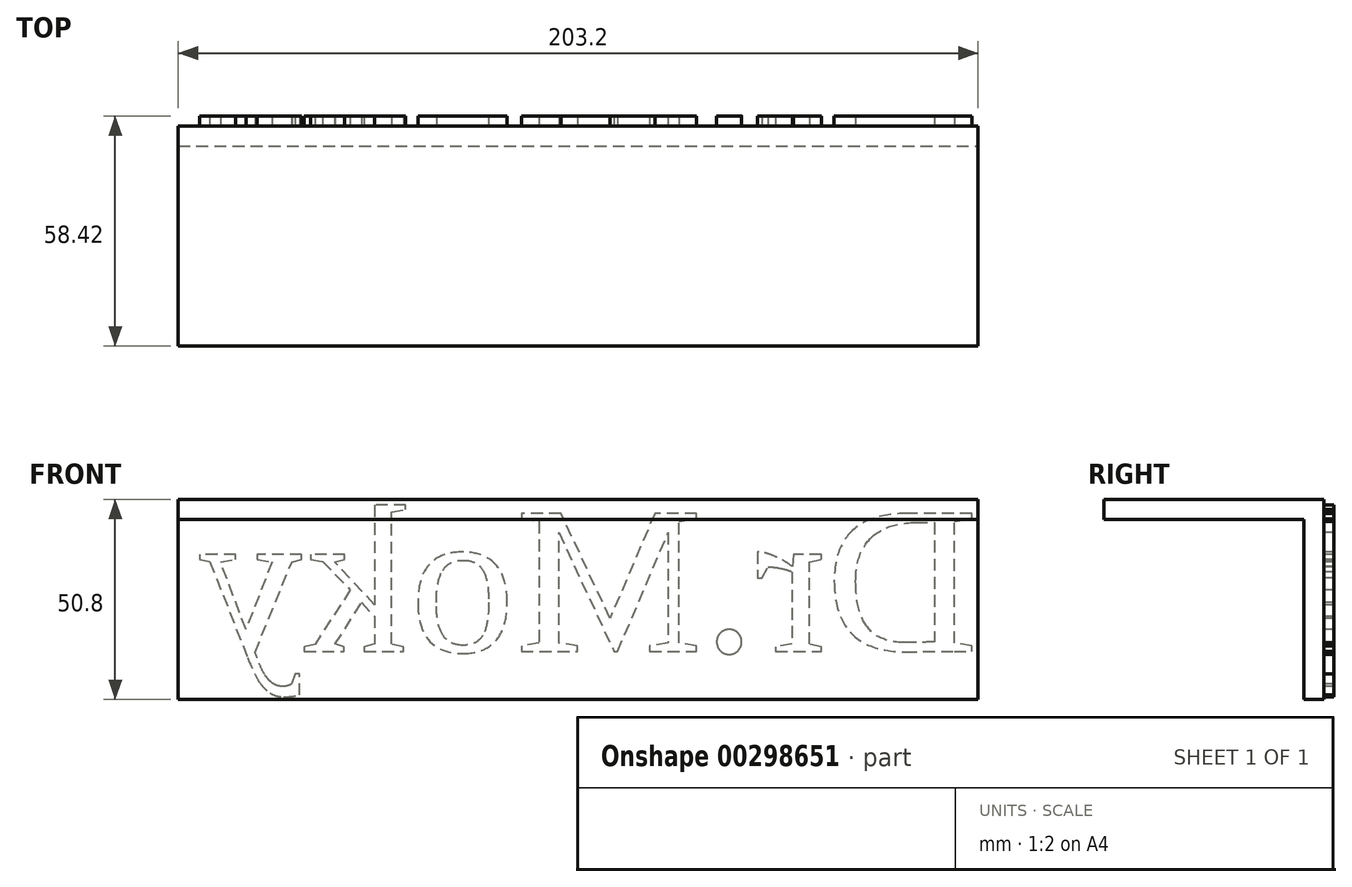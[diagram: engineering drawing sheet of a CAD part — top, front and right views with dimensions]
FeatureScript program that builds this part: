
annotation { "Feature Type Name" : "Feature", "Feature Type Description" : "" }
export const myFeature = defineFeature(function(context is Context, id is Id, definition is map)
    precondition{}
    {
        {
            var Q0;
            Q0=qCreatedBy(makeId("Front.planeOp"),FACE);
            var sketch = newSketch(context, id + "F0", { "sketchPlane" : qUnion([Q0])});
            skLineSegment(sketch, "E0.bottom", {"start": v(-75.83, 25.03) * mm, "end": v(76.57, 25.03) * mm});
            skLineSegment(sketch, "E0.top", {"start": v(-75.83, -25.77) * mm, "end": v(76.57, -25.77) * mm});
            skLineSegment(sketch, "E0.left", {"start": v(-75.83, 25.03) * mm, "end": v(-75.83, -25.77) * mm});
            skLineSegment(sketch, "E0.right", {"start": v(76.57, 25.03) * mm, "end": v(76.57, -25.77) * mm});
            skSolve(sketch);
        }
        {
            var Q0;
            Q0=makeQuery(id+"F0.imprint","IMPRINT",FACE,{"disambiguationData":[TD([[makeQuery(id+"F0.imprint","IMPRINT",EDGE,{"derivedFrom":sQuery(id+"F0.wireOp",EDGE,"E0.bottom")}),-1.0]])]});
            extrude(context, id + "F1", {"entities" : qUnion([Q0]), "depth" : 5.08 * mm});
        }
        {
            var Q0;
            Q0=makeQuery(id+"F1.opExtrude","SWEPT_FACE",FACE,{"disambiguationData":[OSD([sQuery(id+"F0.wireOp",EDGE,"E0.left")])]});
            extrude(context, id + "F2", {"entities" : qUnion([Q0]), "operationType" : NewBodyOperationType.ADD, "depth" : 76.2 * mm});
        }
        {
            var Q0;
            {var subQ0=sQuery(id+"F0.wireOp",EDGE,"E0.left");Q0=makeQuery(id+"F2.boolean.opBoolean","MERGE",FACE,{"derivedFrom":[makeQuery(id+"F1.opExtrude","CAP_FACE",FACE,{"disambiguationData":[OSD([sQuery(id+"F0.wireOp",EDGE,"E0.bottom"),sQuery(id+"F0.wireOp",EDGE,"E0.top"),subQ0,sQuery(id+"F0.wireOp",EDGE,"E0.right")])],"isStart":true}),makeQuery(id+"F2.opExtrude","SWEPT_FACE",FACE,{"disambiguationData":[OSD([subQ0]),TDD([makeQuery(id+"F1.opExtrude","CAP_EDGE",EDGE,{"disambiguationData":[OSD([subQ0])],"isStart":true})])]})]});}
            var sketch = newSketch(context, id + "F3", { "sketchPlane" : qUnion([Q0])});
            skText(sketch, "E1", { "text": "Dr.Moky", "fontName": "Tinos-Regular.ttf"});
            const initialGuessF3  = {"E1": [-0.07657, -0.01356, 1, 0, 0.03858]};
            skSetInitialGuess(sketch, initialGuessF3);
            skSolve(sketch);
        }
        {
            var Q0;
            Q0 = qSketchRegion(id + "F3", true);
            extrude(context, id + "F4", {"entities" : qUnion([Q0]), "operationType" : NewBodyOperationType.ADD, "depth" : 2.54 * mm});
        }
        {
            var Q0;
            Q0=makeQuery(id+"F2.opExtrude","CAP_FACE",FACE,{"disambiguationData":[OSD([sQuery(id+"F0.wireOp",EDGE,"E0.left")])],"isStart":false});
            extrude(context, id + "F5", {"entities" : qUnion([Q0]), "operationType" : NewBodyOperationType.REMOVE, "oppositeDirection" : true, "depth" : 25.4 * mm});
        }
        {
            var Q0;
            {var subQ0=sQuery(id+"F0.wireOp",EDGE,"E0.left");Q0=makeQuery(id+"F2.boolean.opBoolean","MERGE",FACE,{"derivedFrom":[makeQuery(id+"F1.opExtrude","CAP_FACE",FACE,{"disambiguationData":[OSD([sQuery(id+"F0.wireOp",EDGE,"E0.bottom"),sQuery(id+"F0.wireOp",EDGE,"E0.top"),subQ0,sQuery(id+"F0.wireOp",EDGE,"E0.right")])],"isStart":false}),makeQuery(id+"F2.opExtrude","SWEPT_FACE",FACE,{"disambiguationData":[OSD([subQ0]),TDD([makeQuery(id+"F1.opExtrude","CAP_EDGE",EDGE,{"disambiguationData":[OSD([subQ0])],"isStart":false})])]})]});}
            var sketch = newSketch(context, id + "F6", { "sketchPlane" : qUnion([Q0])});
            skLineSegment(sketch, "E2.bottom", {"start": v(-126.63, 25.03) * mm, "end": v(76.57, 25.03) * mm});
            skLineSegment(sketch, "E2.top", {"start": v(-126.63, 19.95) * mm, "end": v(76.57, 19.95) * mm});
            skLineSegment(sketch, "E2.left", {"start": v(-126.63, 25.03) * mm, "end": v(-126.63, 19.95) * mm});
            skLineSegment(sketch, "E2.right", {"start": v(76.57, 25.03) * mm, "end": v(76.57, 19.95) * mm});
            skSolve(sketch);
        }
        {
            var Q0;
            Q0=makeQuery(id+"F6.imprint","IMPRINT",FACE,{"disambiguationData":[TD([[makeQuery(id+"F6.imprint","IMPRINT",EDGE,{"derivedFrom":sQuery(id+"F6.wireOp",EDGE,"E2.bottom")}),-1.0]])]});
            extrude(context, id + "F7", {"entities" : qUnion([Q0]), "operationType" : NewBodyOperationType.ADD, "depth" : 50.8 * mm});
        }
    });
